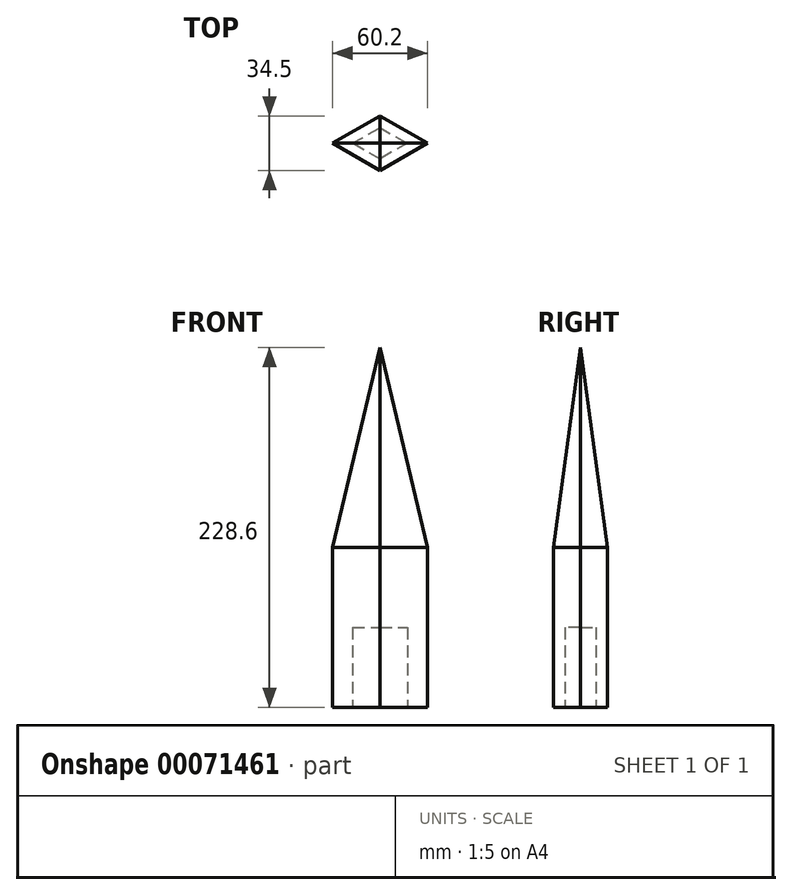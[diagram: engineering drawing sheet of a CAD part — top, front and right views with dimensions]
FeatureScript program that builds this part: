
annotation { "Feature Type Name" : "Feature", "Feature Type Description" : "" }
export const myFeature = defineFeature(function(context is Context, id is Id, definition is map)
    precondition{}
    {
        {
            var Q0;
            Q0=qCreatedBy(makeId("Top.planeOp"),FACE);
            var sketch = newSketch(context, id + "F0", { "sketchPlane" : qUnion([Q0])});
            skLineSegment(sketch, "E0", {"start": v(0, 0) * mm, "end": v(-30.1, 0) * mm});
            skLineSegment(sketch, "E1", {"start": v(0, 0) * mm, "end": v(0, 17.25) * mm});
            skLineSegment(sketch, "E2.MirrorCS", {"start": v(0, 0) * mm, "end": v(30.1, 0) * mm});
            skLineSegment(sketch, "E3.MirrorCS", {"start": v(0, 0) * mm, "end": v(0, -17.25) * mm});
            skLineSegment(sketch, "E4", {"start": v(-30.1, 0) * mm, "end": v(0, 17.25) * mm});
            skLineSegment(sketch, "E5", {"start": v(0, 17.25) * mm, "end": v(30.1, 0) * mm});
            skLineSegment(sketch, "E6", {"start": v(30.1, 0) * mm, "end": v(0, -17.25) * mm});
            skLineSegment(sketch, "E7", {"start": v(0, -17.25) * mm, "end": v(-30.1, 0) * mm});
            skLineSegment(sketch, "E8.0", {"start": v(-17.33, 0) * mm, "end": v(0, 9.93) * mm});
            skLineSegment(sketch, "E8.1", {"start": v(0, -9.93) * mm, "end": v(-17.33, 0) * mm});
            skLineSegment(sketch, "E8.2", {"start": v(17.33, 0) * mm, "end": v(0, -9.93) * mm});
            skLineSegment(sketch, "E8.3", {"start": v(0, 9.93) * mm, "end": v(17.33, 0) * mm});
            skSolve(sketch);
        }
        {
            var Q0;
            {var subQ0=sQuery(id+"F0.wireOp",EDGE,"E5");Q0=makeQuery(id+"F0.imprint","IMPRINT",FACE,{"disambiguationData":[TD([[makeQuery(id+"F0.imprint","IMPRINT",EDGE,{"derivedFrom":subQ0}),-1.0]])]});}
            var Q1;
            {var subQ0=sQuery(id+"F0.wireOp",EDGE,"E4");Q1=makeQuery(id+"F0.imprint","IMPRINT",FACE,{"disambiguationData":[TD([[makeQuery(id+"F0.imprint","IMPRINT",EDGE,{"derivedFrom":subQ0}),-1.0]])]});}
            var Q2;
            {var subQ0=sQuery(id+"F0.wireOp",EDGE,"E7");Q2=makeQuery(id+"F0.imprint","IMPRINT",FACE,{"disambiguationData":[TD([[makeQuery(id+"F0.imprint","IMPRINT",EDGE,{"derivedFrom":subQ0}),-1.0]])]});}
            var Q3;
            {var subQ0=sQuery(id+"F0.wireOp",EDGE,"E6");Q3=makeQuery(id+"F0.imprint","IMPRINT",FACE,{"disambiguationData":[TD([[makeQuery(id+"F0.imprint","IMPRINT",EDGE,{"derivedFrom":subQ0}),-1.0]])]});}
            extrude(context, id + "F1", {"entities" : qUnion([Q0, Q1, Q2, Q3]), "depth" : 50.8 * mm});
        }
        {
            var Q0;
            Q0=makeQuery(id+"F1.opExtrude","CAP_FACE",FACE,{"disambiguationData":[OSD([sQuery(id+"F0.wireOp",EDGE,"E4"),sQuery(id+"F0.wireOp",EDGE,"E5"),sQuery(id+"F0.wireOp",EDGE,"E6"),sQuery(id+"F0.wireOp",EDGE,"E7"),sQuery(id+"F0.wireOp",EDGE,"E8.0"),sQuery(id+"F0.wireOp",EDGE,"E8.1"),sQuery(id+"F0.wireOp",EDGE,"E8.2"),sQuery(id+"F0.wireOp",EDGE,"E8.3")])],"isStart":false});
            var sketch = newSketch(context, id + "F2", { "sketchPlane" : qUnion([Q0])});
            skSolve(sketch);
        }
        {
            var Q0;
            Q0=makeQuery(id+"F2.imprint","IMPRINT",FACE,{"disambiguationData":[TD([[makeQuery(id+"F2.imprint","IMPRINT",EDGE,{"derivedFrom":makeQuery(id+"F1.opExtrude","CAP_EDGE",EDGE,{"disambiguationData":[OSD([sQuery(id+"F0.wireOp",EDGE,"E8.0")])],"isStart":false})}),-1.0]])]});
            var Q1;
            Q1=makeQuery(id+"F2.imprint","IMPRINT",FACE,{"disambiguationData":[TD([[makeQuery(id+"F2.imprint","IMPRINT",EDGE,{"derivedFrom":makeQuery(id+"F1.opExtrude","CAP_EDGE",EDGE,{"disambiguationData":[OSD([sQuery(id+"F0.wireOp",EDGE,"E4")])],"isStart":false})}),-1.0]])]});
            extrude(context, id + "F3", {"entities" : qUnion([Q0, Q1]), "operationType" : NewBodyOperationType.ADD, "depth" : 177.8 * mm});
        }
        {
            var Q0;
            Q0=makeQuery(id+"F3.opExtrude","CAP_FACE",FACE,{"disambiguationData":[OSD([sQuery(id+"F0.wireOp",EDGE,"E4"),sQuery(id+"F0.wireOp",EDGE,"E5"),sQuery(id+"F0.wireOp",EDGE,"E6"),sQuery(id+"F0.wireOp",EDGE,"E7")])],"isStart":false});
            chamfer(context, id + "F4", {"entities" : qUnion([Q0]), "chamferType" : ChamferType.TWO_OFFSETS, "width1" : 127 * mm, "oppositeDirection" : false, "width2" : 14.96 * mm, "tangentPropagation" : true});
        }
    });
